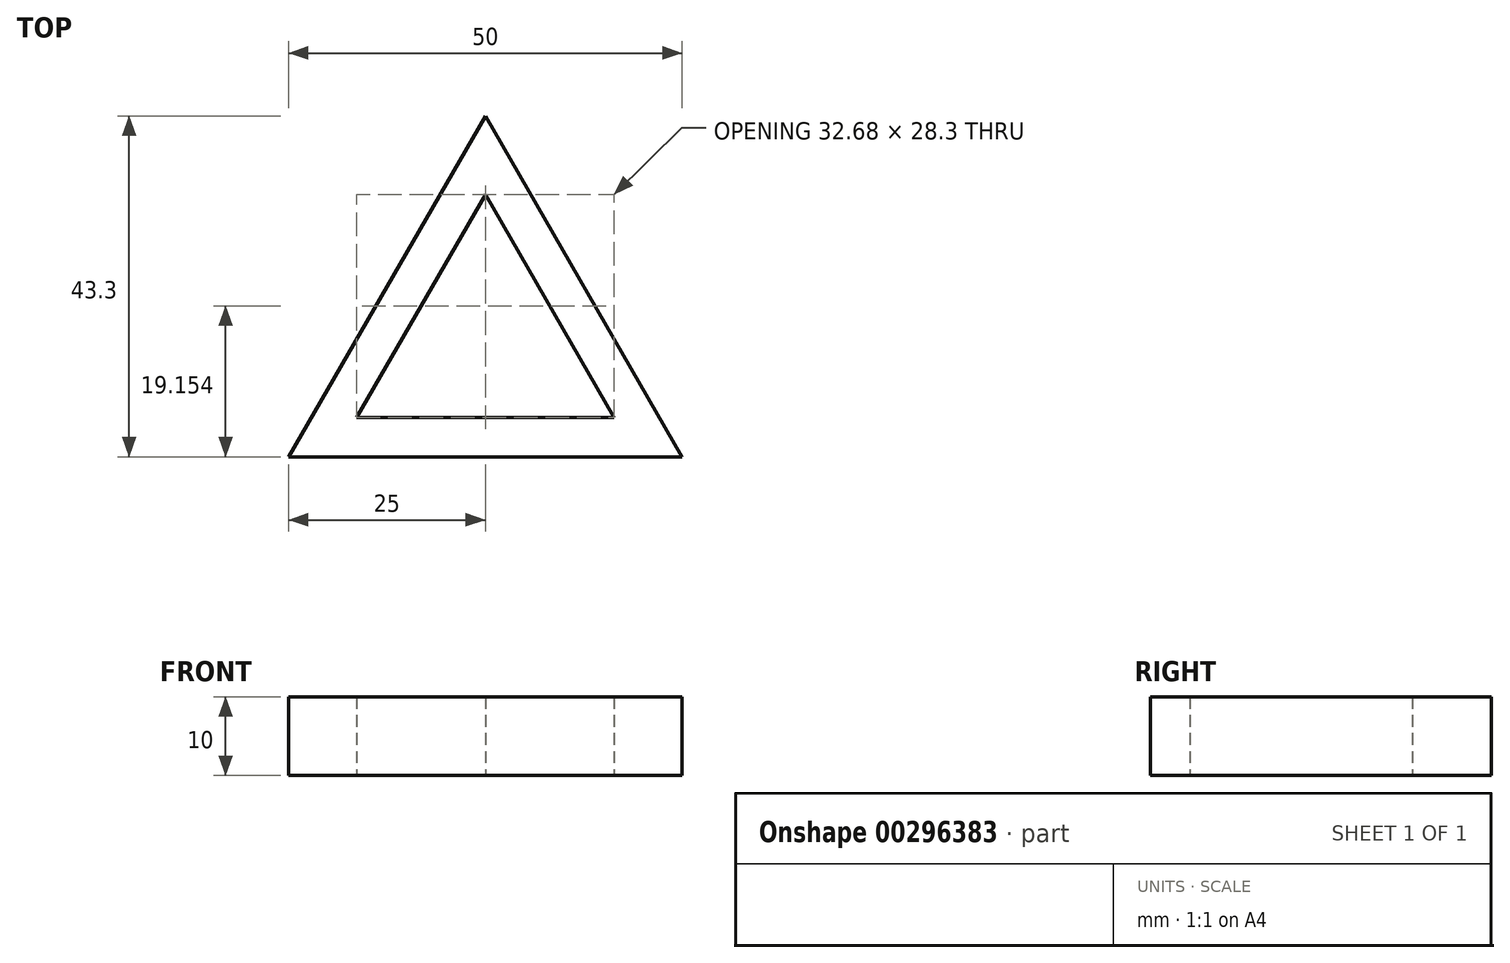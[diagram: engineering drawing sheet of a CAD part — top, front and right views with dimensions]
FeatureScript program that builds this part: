
annotation { "Feature Type Name" : "Feature", "Feature Type Description" : "" }
export const myFeature = defineFeature(function(context is Context, id is Id, definition is map)
    precondition{}
    {
        {
            var Q0;
            Q0=qCreatedBy(makeId("Top.planeOp"),FACE);
            var sketch = newSketch(context, id + "F0", { "sketchPlane" : qUnion([Q0])});
            skLineSegment(sketch, "E0", {"start": v(-25, -14.98) * mm, "end": v(25, -14.98) * mm});
            skLineSegment(sketch, "E1", {"start": v(25, -14.98) * mm, "end": v(0, 28.32) * mm});
            skLineSegment(sketch, "E2", {"start": v(0, 28.32) * mm, "end": v(-25, -14.98) * mm});
            skLineSegment(sketch, "E3.0", {"start": v(-16.34, -9.98) * mm, "end": v(16.34, -9.98) * mm});
            skLineSegment(sketch, "E3.1", {"start": v(0, 18.32) * mm, "end": v(-16.34, -9.98) * mm});
            skLineSegment(sketch, "E3.2", {"start": v(16.34, -9.98) * mm, "end": v(0, 18.32) * mm});
            skSolve(sketch);
        }
        {
            var Q0;
            Q0=makeQuery(id+"F0.imprint","IMPRINT",FACE,{"disambiguationData":[TD([[makeQuery(id+"F0.imprint","IMPRINT",EDGE,{"derivedFrom":sQuery(id+"F0.wireOp",EDGE,"E0")}),1.0]])]});
            extrude(context, id + "F1", {"entities" : qUnion([Q0]), "depth" : 10 * mm});
        }
    });
